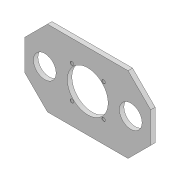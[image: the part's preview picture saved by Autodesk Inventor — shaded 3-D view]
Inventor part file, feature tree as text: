
AUTODESK INVENTOR PART (.ipt)
format: ipt  version: 2020 (Build 240168000, 168)  size: 142,848 bytes
history: native  units: mm
features: sketch x2, extrude x1, hole x1, chamfer x1, projected_geometry x1
ambient origin geometry x8: Origin, YZ Plane, XZ Plane, XY Plane, X Axis, Y Axis, Z Axis, Center Point
bodies: Body1 (feature_tree)
feature tree (6):
  extrude  "Extrusion2"  Depth=168.0mm
  hole  "Hole1"  [1 undecoded]
  chamfer  "Chamfer2"  Distance=95.0mm
  sketch  "Sketch1"  dims[d0=278.0mm d1=168.0mm]
  sketch  "Sketch2"  dims[d8=50.0mm d9=190.0mm d10=95.0mm d11=90.0mm d12=50.0mm d13=50.0mm d14=50.0mm d15=50.0mm d16=50.0mm d17=50.0mm d18=50.0mm d19=50.0mm d20=10.0mm d21=0.0mm d22=70.0mm d23=6.647mm d24=10.0mm d25=4.0mm d26=2.0mm d27=90.0deg d28=22.2mm d29=20.594885mm d30=0.5mm d31=2.0mm d32=45.0deg]
  projected_geometry  "Projected Loop1"
note: 1 required parameter value undecoded (feature->parameter linkage not recoverable at this tier; creation-order binding heuristic only, values carry confidence <= 0.55)
